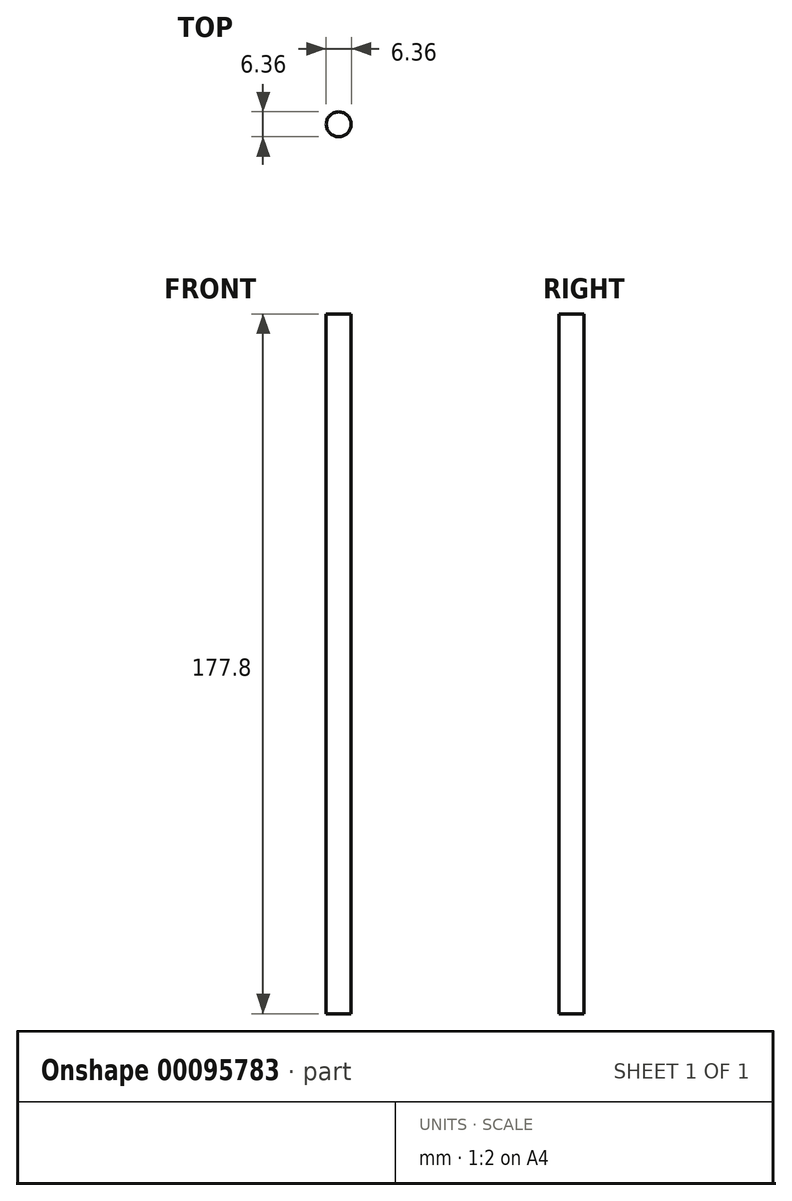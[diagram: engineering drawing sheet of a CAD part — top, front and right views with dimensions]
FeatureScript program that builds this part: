
annotation { "Feature Type Name" : "Feature", "Feature Type Description" : "" }
export const myFeature = defineFeature(function(context is Context, id is Id, definition is map)
    precondition{}
    {
        {
            var Q0;
            Q0=qCreatedBy(makeId("Top.planeOp"),FACE);
            var sketch = newSketch(context, id + "F0", { "sketchPlane" : qUnion([Q0])});
            skCircle(sketch, "E0", {"center": v(0, 0) * mm, "radius": 3.18 * mm});
            skSolve(sketch);
        }
        {
            var Q0;
            Q0=makeQuery(id+"F0.imprint","IMPRINT",FACE,{"disambiguationData":[TD([[makeQuery(id+"F0.imprint","IMPRINT",EDGE,{"derivedFrom":sQuery(id+"F0.wireOp",EDGE,"E0")}),1.0]])]});
            extrude(context, id + "F1", {"entities" : qUnion([Q0]), "endBound" : BoundingType.SYMMETRIC, "depth" : 177.8 * mm});
        }
    });
